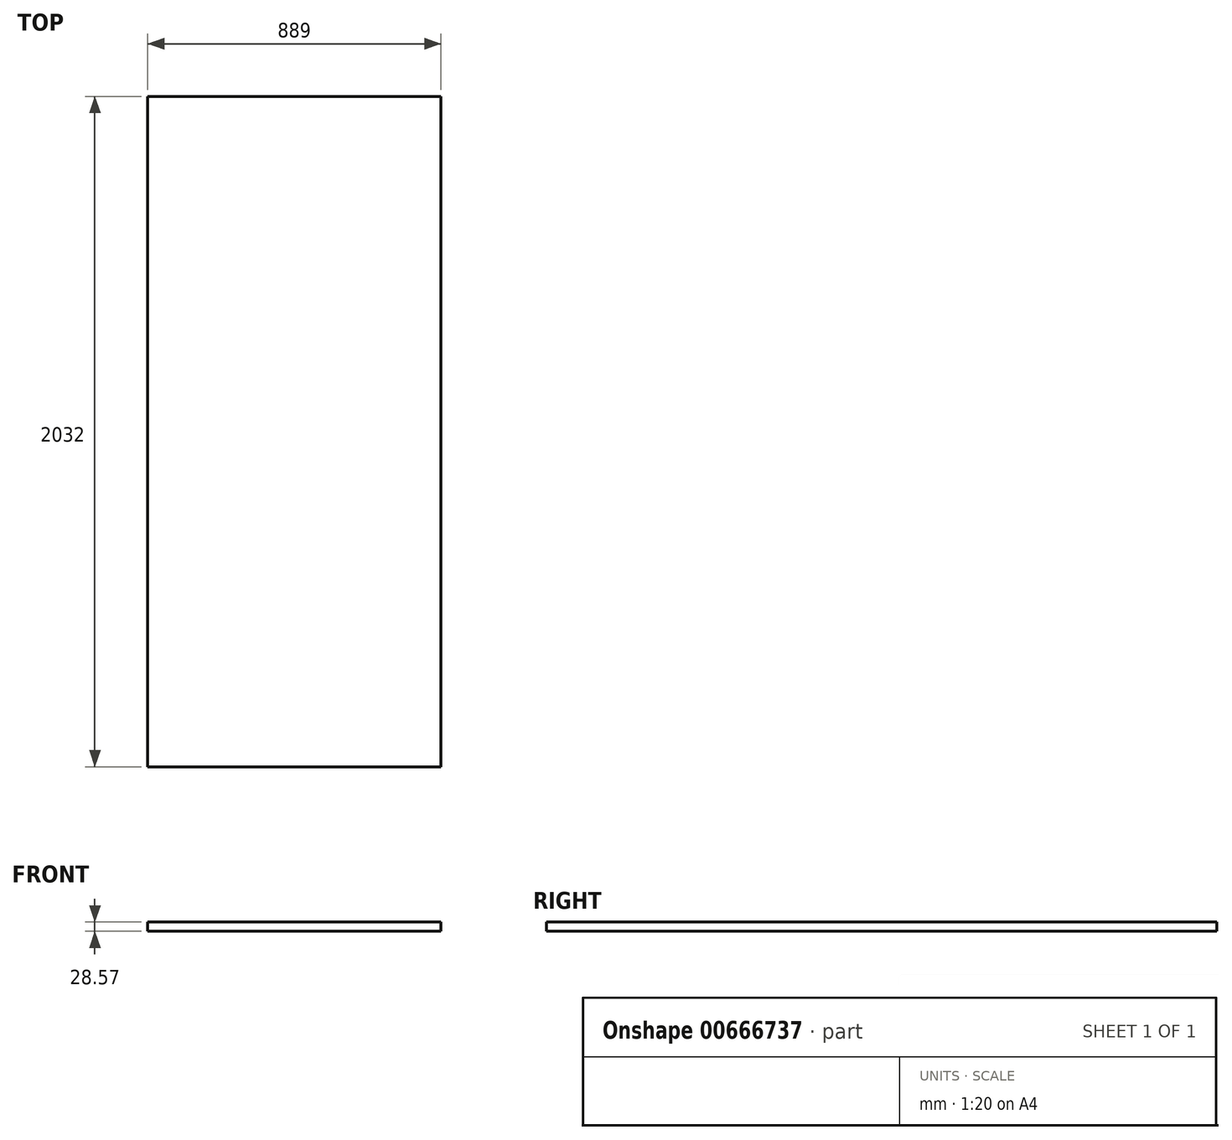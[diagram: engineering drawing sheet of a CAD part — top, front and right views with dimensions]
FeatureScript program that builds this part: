
annotation { "Feature Type Name" : "Feature", "Feature Type Description" : "" }
export const myFeature = defineFeature(function(context is Context, id is Id, definition is map)
    precondition{}
    {
        {
            var Q0;
            Q0=qCreatedBy(makeId("Top.planeOp"),FACE);
            var sketch = newSketch(context, id + "F0", { "sketchPlane" : qUnion([Q0])});
            skLineSegment(sketch, "E0.bottom", {"start": v(444.5, 1016) * mm, "end": v(-444.5, 1016) * mm});
            skLineSegment(sketch, "E0.top", {"start": v(444.5, -1016) * mm, "end": v(-444.5, -1016) * mm});
            skLineSegment(sketch, "E0.left", {"start": v(444.5, 1016) * mm, "end": v(444.5, -1016) * mm});
            skLineSegment(sketch, "E0.right", {"start": v(-444.5, 1016) * mm, "end": v(-444.5, -1016) * mm});
            skPoint(sketch, "E0.middle", {"position": v(0, 0) * mm});
            skSolve(sketch);
        }
        {
            var Q0;
            Q0=makeQuery(id+"F0.imprint","IMPRINT",FACE,{"disambiguationData":[TD([[makeQuery(id+"F0.imprint","IMPRINT",EDGE,{"derivedFrom":sQuery(id+"F0.wireOp",EDGE,"E0.bottom")}),1.0]])]});
            extrude(context, id + "F1", {"entities" : qUnion([Q0]), "depth" : 28.57 * mm, "offsetDistance" : 25.4 * mm});
        }
    });
